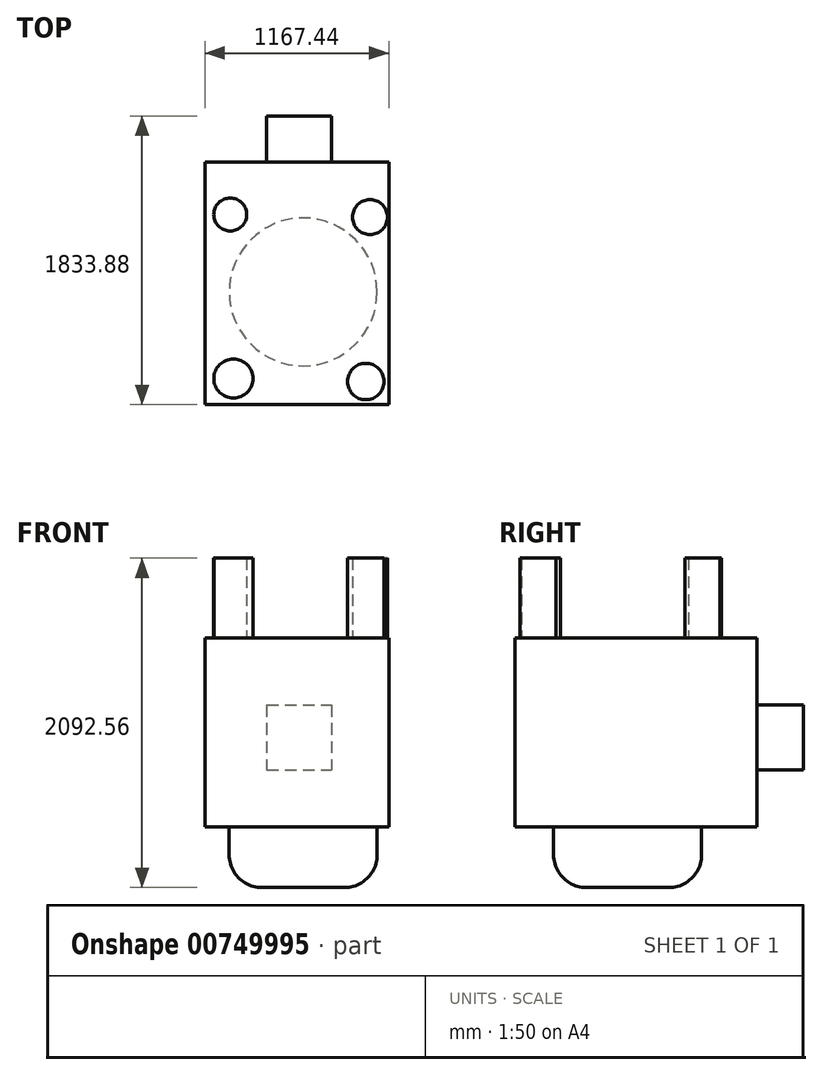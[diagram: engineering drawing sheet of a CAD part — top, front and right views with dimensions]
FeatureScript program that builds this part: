
annotation { "Feature Type Name" : "Feature", "Feature Type Description" : "" }
export const myFeature = defineFeature(function(context is Context, id is Id, definition is map)
    precondition{}
    {
        {
            var Q0;
            Q0=qCreatedBy(makeId("Front.planeOp"),FACE);
            var sketch = newSketch(context, id + "F0", { "sketchPlane" : qUnion([Q0])});
            skLineSegment(sketch, "E0.bottom", {"start": v(-511.99, -79.28) * mm, "end": v(655.45, -79.28) * mm});
            skLineSegment(sketch, "E0.top", {"start": v(-511.99, -1277.76) * mm, "end": v(655.45, -1277.76) * mm});
            skLineSegment(sketch, "E0.left", {"start": v(-511.99, -79.28) * mm, "end": v(-511.99, -1277.76) * mm});
            skLineSegment(sketch, "E0.right", {"start": v(655.45, -79.28) * mm, "end": v(655.45, -1277.76) * mm});
            skSolve(sketch);
        }
        {
            var Q0;
            Q0 = qSketchRegion(id + "F0", true);
            extrude(context, id + "F1", {"entities" : qUnion([Q0]), "depth" : 1539.24 * mm, "offsetDistance" : 25.4 * mm});
        }
        {
            var Q0;
            Q0=makeQuery(id+"F1.opExtrude","SWEPT_FACE",FACE,{"disambiguationData":[OSD([sQuery(id+"F0.wireOp",EDGE,"E0.bottom")])]});
            var sketch = newSketch(context, id + "F2", { "sketchPlane" : qUnion([Q0])});
            skPoint(sketch, "E1", {"position": v(508.97, -1392.53) * mm});
            skPoint(sketch, "E2", {"position": v(535.52, -348.27) * mm});
            skPoint(sketch, "E3", {"position": v(-352.23, -331.84) * mm});
            skCircle(sketch, "E4", {"center": v(-352.23, -331.84) * mm, "radius": 104.85 * mm});
            skCircle(sketch, "E5", {"center": v(535.52, -348.27) * mm, "radius": 110.9 * mm});
            skCircle(sketch, "E6", {"center": v(508.97, -1392.53) * mm, "radius": 115.64 * mm});
            skSolve(sketch);
        }
        {
            var Q0;
            Q0=makeQuery(id+"F2.imprint","IMPRINT",FACE,{"disambiguationData":[TD([[makeQuery(id+"F2.imprint","IMPRINT",EDGE,{"derivedFrom":sQuery(id+"F2.wireOp",EDGE,"E4")}),-1.0]])]});
            var sketch = newSketch(context, id + "F3", { "sketchPlane" : qUnion([Q0])});
            skPoint(sketch, "E7", {"position": v(-332.12, -1373.2) * mm});
            skCircle(sketch, "E8", {"center": v(-332.12, -1373.2) * mm, "radius": 123.91 * mm});
            skSolve(sketch);
        }
        {
            var Q0;
            Q0 = qSketchRegion(id + "F3", true);
            var Q1;
            Q1=makeQuery(id+"F2.imprint","IMPRINT",FACE,{"disambiguationData":[TD([[makeQuery(id+"F2.imprint","IMPRINT",EDGE,{"derivedFrom":sQuery(id+"F2.wireOp",EDGE,"E4")}),1.0]])]});
            var Q2;
            Q2=makeQuery(id+"F3.imprint","IMPRINT",FACE,{"disambiguationData":[TD([[makeQuery(id+"F3.imprint","IMPRINT",EDGE,{"derivedFrom":makeQuery(id+"F2.imprint","IMPRINT",EDGE,{"derivedFrom":sQuery(id+"F2.wireOp",EDGE,"E5")})}),1.0]])]});
            var Q3;
            Q3=makeQuery(id+"F3.imprint","IMPRINT",FACE,{"disambiguationData":[TD([[makeQuery(id+"F3.imprint","IMPRINT",EDGE,{"derivedFrom":makeQuery(id+"F2.imprint","IMPRINT",EDGE,{"derivedFrom":sQuery(id+"F2.wireOp",EDGE,"E6")})}),1.0]])]});
            extrude(context, id + "F4", {"entities" : qUnion([Q0, Q1, Q2, Q3]), "operationType" : NewBodyOperationType.ADD, "depth" : 508 * mm, "offsetDistance" : 25.4 * mm});
        }
        {
            var Q0;
            Q0=makeQuery(id+"F1.opExtrude","CAP_FACE",FACE,{"disambiguationData":[OSD([sQuery(id+"F0.wireOp",EDGE,"E0.bottom"),sQuery(id+"F0.wireOp",EDGE,"E0.top"),sQuery(id+"F0.wireOp",EDGE,"E0.left"),sQuery(id+"F0.wireOp",EDGE,"E0.right")])],"isStart":true});
            var sketch = newSketch(context, id + "F5", { "sketchPlane" : qUnion([Q0])});
            skPoint(sketch, "E9", {"position": v(-84.96, -709.48) * mm});
            skLineSegment(sketch, "E10.bottom", {"start": v(120.42, -504.1) * mm, "end": v(-290.34, -504.1) * mm});
            skLineSegment(sketch, "E10.top", {"start": v(120.42, -914.86) * mm, "end": v(-290.34, -914.86) * mm});
            skLineSegment(sketch, "E10.left", {"start": v(120.42, -504.1) * mm, "end": v(120.42, -914.86) * mm});
            skLineSegment(sketch, "E10.right", {"start": v(-290.34, -504.1) * mm, "end": v(-290.34, -914.86) * mm});
            skSolve(sketch);
        }
        {
            var Q0;
            Q0=makeQuery(id+"F5.imprint","IMPRINT",FACE,{"disambiguationData":[TD([[makeQuery(id+"F5.imprint","IMPRINT",EDGE,{"derivedFrom":sQuery(id+"F5.wireOp",EDGE,"E10.bottom")}),1.0]])]});
            extrude(context, id + "F6", {"entities" : qUnion([Q0]), "operationType" : NewBodyOperationType.ADD, "depth" : 294.64 * mm, "offsetDistance" : 25.4 * mm});
        }
        {
            var Q0;
            Q0=makeQuery(id+"F1.opExtrude","SWEPT_FACE",FACE,{"disambiguationData":[OSD([sQuery(id+"F0.wireOp",EDGE,"E0.top")])]});
            var sketch = newSketch(context, id + "F7", { "sketchPlane" : qUnion([Q0])});
            skPoint(sketch, "E11", {"position": v(110.9, 823.16) * mm});
            skCircle(sketch, "E12", {"center": v(110.9, 823.16) * mm, "radius": 469.83 * mm});
            skSolve(sketch);
        }
        {
            var Q0;
            Q0=makeQuery(id+"F7.imprint","IMPRINT",FACE,{"disambiguationData":[TD([[makeQuery(id+"F7.imprint","IMPRINT",EDGE,{"derivedFrom":sQuery(id+"F7.wireOp",EDGE,"E12")}),1.0]])]});
            extrude(context, id + "F8", {"entities" : qUnion([Q0]), "operationType" : NewBodyOperationType.ADD, "depth" : 386.08 * mm, "offsetDistance" : 25.4 * mm});
        }
        {
            var Q0;
            Q0=makeQuery(id+"F8.opExtrude","CAP_FACE",FACE,{"disambiguationData":[OSD([sQuery(id+"F7.wireOp",EDGE,"E12")])],"isStart":false});
            fillet(context, id + "F9", {"entities" : qUnion([Q0]), "radius" : 208.5 * mm, "tangentPropagation" : true, "allowEdgeOverflow" : false});
        }
    });
